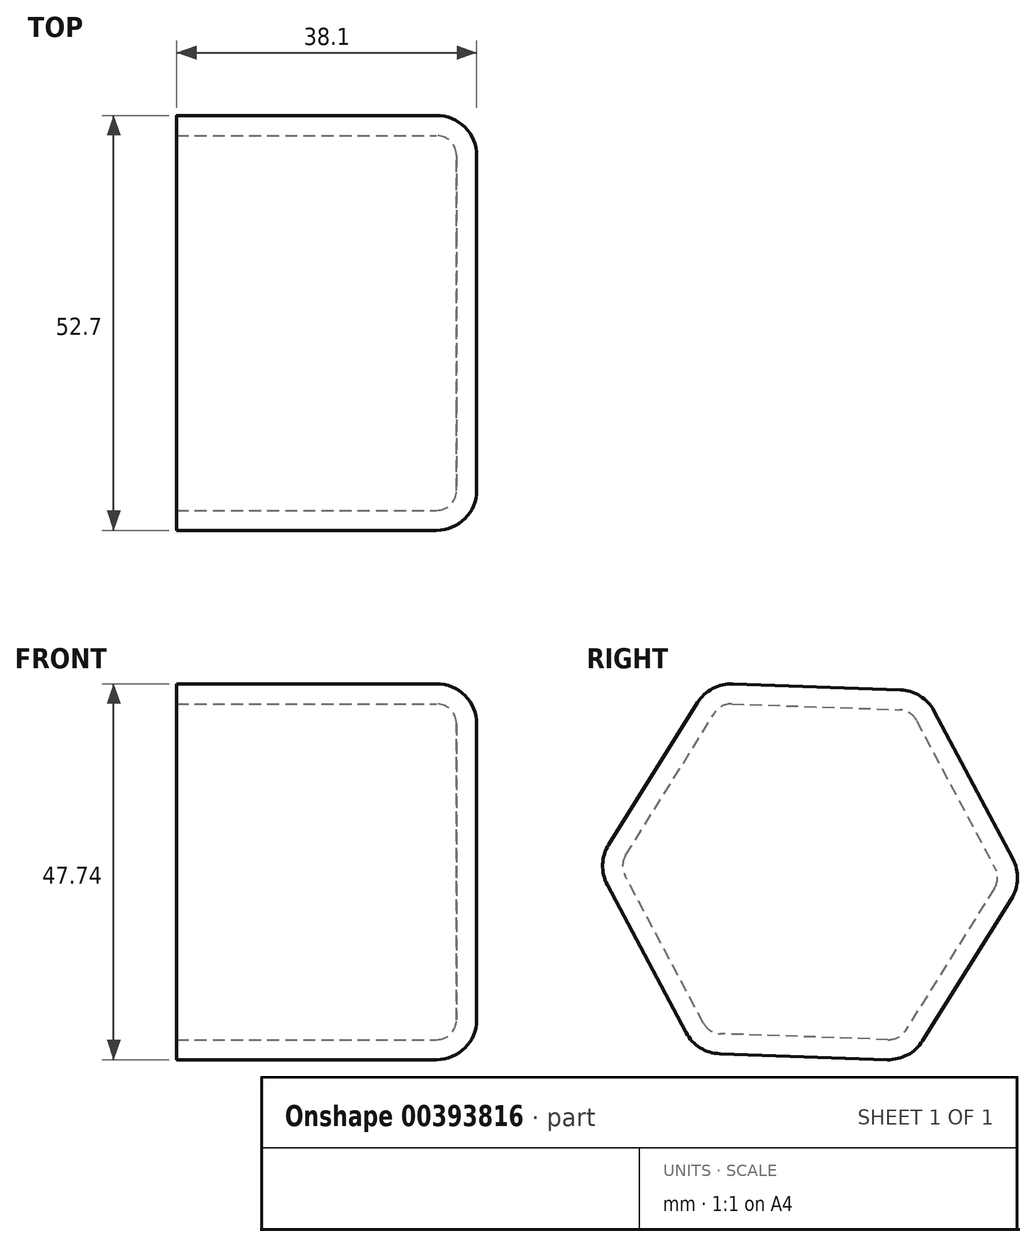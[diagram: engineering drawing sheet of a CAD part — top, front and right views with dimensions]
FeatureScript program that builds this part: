
annotation { "Feature Type Name" : "Feature", "Feature Type Description" : "" }
export const myFeature = defineFeature(function(context is Context, id is Id, definition is map)
    precondition{}
    {
        {
            var Q0;
            Q0=qCreatedBy(makeId("Right.planeOp"),FACE);
            var sketch = newSketch(context, id + "F0", { "sketchPlane" : qUnion([Q0])});
            skCircle(sketch, "E0.cCircle", {"center": v(0, 0) * mm, "radius": 23.5 * mm, "construction": true});
            skLineSegment(sketch, "E0.0", {"start": v(27.13, -0.95) * mm, "end": v(12.75, -23.97) * mm});
            skLineSegment(sketch, "E0.1", {"start": v(12.75, -23.97) * mm, "end": v(-14.38, -23.02) * mm});
            skLineSegment(sketch, "E0.2", {"start": v(-14.38, -23.02) * mm, "end": v(-27.13, 0.95) * mm});
            skLineSegment(sketch, "E0.3", {"start": v(-27.13, 0.95) * mm, "end": v(-12.75, 23.97) * mm});
            skLineSegment(sketch, "E0.4", {"start": v(-12.75, 23.97) * mm, "end": v(14.38, 23.02) * mm});
            skLineSegment(sketch, "E0.5", {"start": v(14.38, 23.02) * mm, "end": v(27.13, -0.95) * mm});
            skPoint(sketch, "E0.0.midPoint", {"position": v(19.94, -12.46) * mm});
            skLineSegment(sketch, "E1", {"start": v(0, 0) * mm, "end": v(0, 0) * mm});
            skSolve(sketch);
        }
        {
            var Q0;
            Q0=makeQuery(id+"F0.imprint","IMPRINT",FACE,{"disambiguationData":[TD([[makeQuery(id+"F0.imprint","IMPRINT",EDGE,{"derivedFrom":sQuery(id+"F0.wireOp",EDGE,"E0.0")}),-1.0]])]});
            extrude(context, id + "F1", {"entities" : qUnion([Q0]), "oppositeDirection" : true, "depth" : 38.1 * mm});
        }
        {
            var Q0;
            Q0=makeQuery(id+"F1.opExtrude","SWEPT_EDGE",EDGE,{"disambiguationData":[OSD([sQuery(id+"F0.wireOp",EDGE,"E0.3"),sQuery(id+"F0.wireOp",EDGE,"E0.4")])]});
            var Q1;
            Q1=makeQuery(id+"F1.opExtrude","SWEPT_EDGE",EDGE,{"disambiguationData":[OSD([sQuery(id+"F0.wireOp",EDGE,"E0.2"),sQuery(id+"F0.wireOp",EDGE,"E0.3")])]});
            var Q2;
            Q2=makeQuery(id+"F1.opExtrude","SWEPT_EDGE",EDGE,{"disambiguationData":[OSD([sQuery(id+"F0.wireOp",EDGE,"E0.4"),sQuery(id+"F0.wireOp",EDGE,"E0.5")])]});
            var Q3;
            Q3=makeQuery(id+"F1.opExtrude","SWEPT_EDGE",EDGE,{"disambiguationData":[OSD([sQuery(id+"F0.wireOp",EDGE,"E0.0"),sQuery(id+"F0.wireOp",EDGE,"E0.1")])]});
            var Q4;
            Q4=makeQuery(id+"F1.opExtrude","SWEPT_EDGE",EDGE,{"disambiguationData":[OSD([sQuery(id+"F0.wireOp",EDGE,"E0.0"),sQuery(id+"F0.wireOp",EDGE,"E0.5")])]});
            var Q5;
            Q5=makeQuery(id+"F1.opExtrude","SWEPT_EDGE",EDGE,{"disambiguationData":[OSD([sQuery(id+"F0.wireOp",EDGE,"E0.1"),sQuery(id+"F0.wireOp",EDGE,"E0.2")])]});
            var Q6;
            Q6=makeQuery(id+"F1.opExtrude","CAP_FACE",FACE,{"disambiguationData":[OSD([sQuery(id+"F0.wireOp",EDGE,"E0.0"),sQuery(id+"F0.wireOp",EDGE,"E0.1"),sQuery(id+"F0.wireOp",EDGE,"E0.2"),sQuery(id+"F0.wireOp",EDGE,"E0.3"),sQuery(id+"F0.wireOp",EDGE,"E0.4"),sQuery(id+"F0.wireOp",EDGE,"E0.5")])],"isStart":true});
            fillet(context, id + "F2", {"entities" : qUnion([Q0, Q1, Q2, Q3, Q4, Q5, Q6]), "radius" : 5.08 * mm, "tangentPropagation" : true, "allowEdgeOverflow" : false});
        }
        {
            var Q0;
            Q0=makeQuery(id+"F1.opExtrude","CAP_FACE",FACE,{"disambiguationData":[OSD([sQuery(id+"F0.wireOp",EDGE,"E0.0"),sQuery(id+"F0.wireOp",EDGE,"E0.1"),sQuery(id+"F0.wireOp",EDGE,"E0.2"),sQuery(id+"F0.wireOp",EDGE,"E0.3"),sQuery(id+"F0.wireOp",EDGE,"E0.4"),sQuery(id+"F0.wireOp",EDGE,"E0.5")])],"isStart":false});
            shell(context, id + "F3", {"entities" : qUnion([Q0]), "thickness" : 2.54 * mm});
        }
    });
